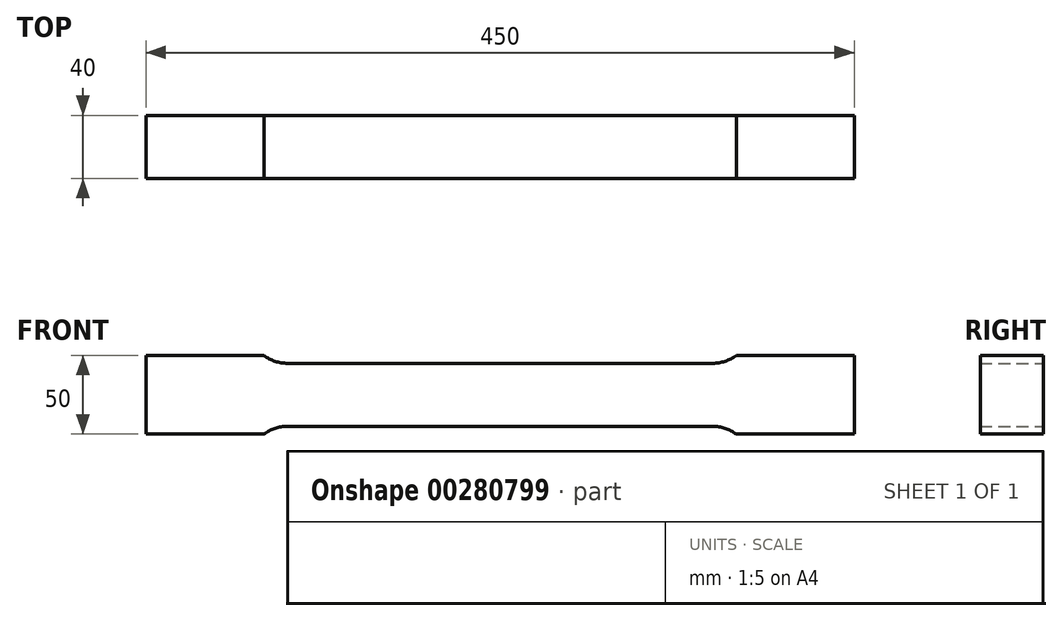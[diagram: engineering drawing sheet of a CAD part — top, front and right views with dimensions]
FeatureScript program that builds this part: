
annotation { "Feature Type Name" : "Feature", "Feature Type Description" : "" }
export const myFeature = defineFeature(function(context is Context, id is Id, definition is map)
    precondition{}
    {
        {
            var Q0;
            Q0=qCreatedBy(makeId("Front.planeOp"),FACE);
            var sketch = newSketch(context, id + "F0", { "sketchPlane" : qUnion([Q0])});
            skLineSegment(sketch, "E0", {"start": v(0, 20) * mm, "end": v(135, 20) * mm});
            skArc(sketch, "E1", {"start": v(135, 20) * mm, "mid": v(142.9, 21.28) * mm, "end": v(150, 25) * mm});
            skLineSegment(sketch, "E2", {"start": v(150, 25) * mm, "end": v(225, 25) * mm});
            skArc(sketch, "E3.MirrorCS", {"start": v(135, -20) * mm, "mid": v(142.9, -21.28) * mm, "end": v(150, -25) * mm});
            skLineSegment(sketch, "E4.MirrorCS", {"start": v(0, -20) * mm, "end": v(135, -20) * mm});
            skLineSegment(sketch, "E5.MirrorCS", {"start": v(150, -25) * mm, "end": v(225, -25) * mm});
            skLineSegment(sketch, "E6", {"start": v(225, 25) * mm, "end": v(225, -25) * mm});
            skLineSegment(sketch, "E7.MirrorCS", {"start": v(0, 20) * mm, "end": v(-135, 20) * mm});
            skArc(sketch, "E8.MirrorCS", {"start": v(-135, 20) * mm, "mid": v(-142.9, 21.28) * mm, "end": v(-150, 25) * mm});
            skLineSegment(sketch, "E9.MirrorCS", {"start": v(-150, 25) * mm, "end": v(-225, 25) * mm});
            skArc(sketch, "E10.MirrorCS", {"start": v(-135, -20) * mm, "mid": v(-142.9, -21.28) * mm, "end": v(-150, -25) * mm});
            skLineSegment(sketch, "E11.MirrorCS", {"start": v(0, -20) * mm, "end": v(-135, -20) * mm});
            skLineSegment(sketch, "E12.MirrorCS", {"start": v(-150, -25) * mm, "end": v(-225, -25) * mm});
            skLineSegment(sketch, "E13.MirrorCS", {"start": v(-225, 25) * mm, "end": v(-225, -25) * mm});
            skSolve(sketch);
        }
        {
            var Q0;
            Q0=makeQuery(id+"F0.imprint","IMPRINT",FACE,{"disambiguationData":[TD([[makeQuery(id+"F0.imprint","IMPRINT",EDGE,{"derivedFrom":sQuery(id+"F0.wireOp",EDGE,"E0")}),-1.0]])]});
            extrude(context, id + "F1", {"entities" : qUnion([Q0]), "endBound" : BoundingType.SYMMETRIC, "depth" : 40 * mm});
        }
    });
